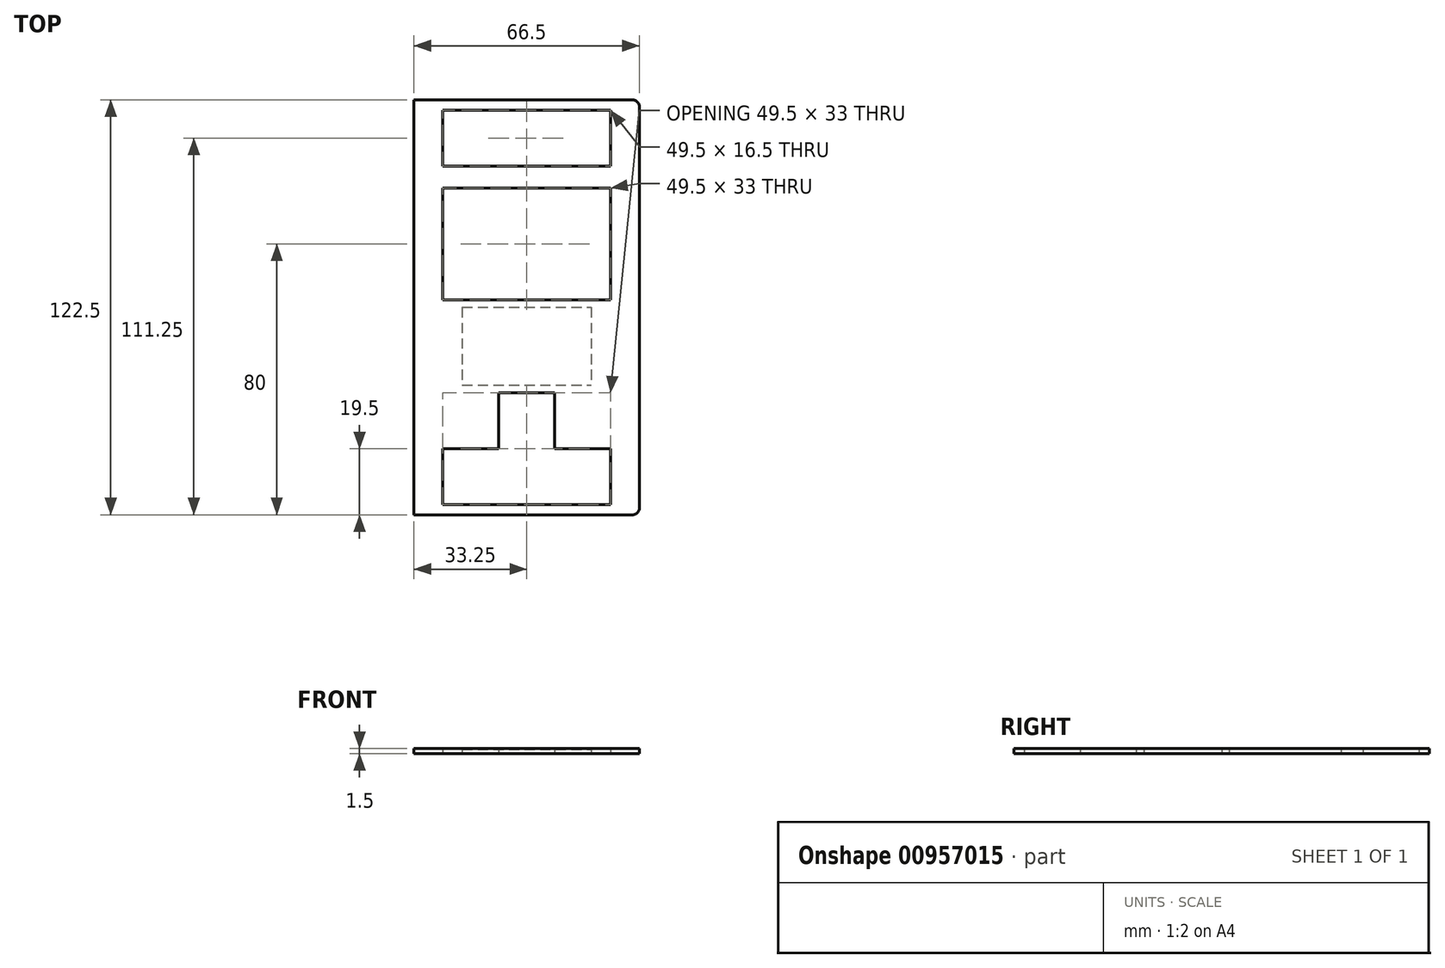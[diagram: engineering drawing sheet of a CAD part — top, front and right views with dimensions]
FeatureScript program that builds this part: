
annotation { "Feature Type Name" : "Feature", "Feature Type Description" : "" }
export const myFeature = defineFeature(function(context is Context, id is Id, definition is map)
    precondition{}
    {
        {
            var Q0;
            Q0=qCreatedBy(makeId("Top.planeOp"),FACE);
            var sketch = newSketch(context, id + "F0", { "sketchPlane" : qUnion([Q0])});
            skLineSegment(sketch, "E0.bottom", {"start": v(33.25, 61.25) * mm, "end": v(-33.25, 61.25) * mm});
            skLineSegment(sketch, "E0.top", {"start": v(33.25, -61.25) * mm, "end": v(-33.25, -61.25) * mm});
            skLineSegment(sketch, "E0.left", {"start": v(33.25, 61.25) * mm, "end": v(33.25, -61.25) * mm});
            skLineSegment(sketch, "E0.right", {"start": v(-33.25, 61.25) * mm, "end": v(-33.25, -61.25) * mm});
            skPoint(sketch, "E0.middle", {"position": v(0, 0) * mm});
            skLineSegment(sketch, "E1", {"start": v(0, -61.25) * mm, "end": v(0, -58.25) * mm});
            skLineSegment(sketch, "E2", {"start": v(0, -58.25) * mm, "end": v(24.75, -58.25) * mm});
            skLineSegment(sketch, "E3", {"start": v(0, -58.25) * mm, "end": v(-24.75, -58.25) * mm});
            skLineSegment(sketch, "E4", {"start": v(-24.75, -58.25) * mm, "end": v(-24.75, -41.75) * mm});
            skLineSegment(sketch, "E5", {"start": v(24.75, -58.25) * mm, "end": v(24.75, -41.75) * mm});
            skLineSegment(sketch, "E6", {"start": v(24.75, -41.75) * mm, "end": v(8.25, -41.75) * mm});
            skLineSegment(sketch, "E7", {"start": v(8.25, -41.75) * mm, "end": v(8.25, -25.25) * mm});
            skLineSegment(sketch, "E8", {"start": v(8.25, -25.25) * mm, "end": v(-8.25, -25.25) * mm});
            skLineSegment(sketch, "E9", {"start": v(-8.25, -25.25) * mm, "end": v(-8.25, -41.75) * mm});
            skLineSegment(sketch, "E10", {"start": v(-8.25, -41.75) * mm, "end": v(-24.75, -41.75) * mm});
            skLineSegment(sketch, "E11", {"start": v(0, 61.25) * mm, "end": v(0, 58.25) * mm});
            skLineSegment(sketch, "E12", {"start": v(0, 58.25) * mm, "end": v(-24.75, 58.25) * mm});
            skLineSegment(sketch, "E13", {"start": v(-24.75, 58.25) * mm, "end": v(-24.75, 41.75) * mm});
            skLineSegment(sketch, "E14", {"start": v(0, 58.25) * mm, "end": v(24.75, 58.25) * mm});
            skLineSegment(sketch, "E15", {"start": v(24.75, 58.25) * mm, "end": v(24.75, 41.75) * mm});
            skLineSegment(sketch, "E16", {"start": v(24.75, 41.75) * mm, "end": v(-24.75, 41.75) * mm});
            skLineSegment(sketch, "E17", {"start": v(0, 41.75) * mm, "end": v(0, 35.25) * mm});
            skLineSegment(sketch, "E18", {"start": v(0, 35.25) * mm, "end": v(-24.75, 35.25) * mm});
            skLineSegment(sketch, "E19", {"start": v(-24.75, 35.25) * mm, "end": v(-24.75, 2.25) * mm});
            skLineSegment(sketch, "E20", {"start": v(-24.75, 2.25) * mm, "end": v(24.75, 2.25) * mm});
            skLineSegment(sketch, "E21", {"start": v(24.75, 2.25) * mm, "end": v(24.75, 35.25) * mm});
            skLineSegment(sketch, "E22", {"start": v(24.75, 35.25) * mm, "end": v(0, 35.25) * mm});
            skSolve(sketch);
        }
        {
            var Q0;
            {var subQ7=sQuery(id+"F0.wireOp",EDGE,"E0.left");Q0=makeQuery(id+"F0.imprint","IMPRINT",FACE,{"disambiguationData":[TD([[makeQuery(id+"F0.imprint","IMPRINT",EDGE,{"derivedFrom":subQ7}),-1.0]])]});}
            extrude(context, id + "F1", {"entities" : qUnion([Q0]), "depth" : 1.5 * mm, "offsetDistance" : 25 * mm});
        }
        {
            var Q0;
            Q0=makeQuery(id+"F1.opExtrude","CAP_FACE",FACE,{"disambiguationData":[OSD([sQuery(id+"F0.wireOp",EDGE,"E0.bottom"),sQuery(id+"F0.wireOp",EDGE,"E0.top"),sQuery(id+"F0.wireOp",EDGE,"E0.left"),sQuery(id+"F0.wireOp",EDGE,"E0.right"),sQuery(id+"F0.wireOp",EDGE,"E2"),sQuery(id+"F0.wireOp",EDGE,"E3"),sQuery(id+"F0.wireOp",EDGE,"E4"),sQuery(id+"F0.wireOp",EDGE,"E5"),sQuery(id+"F0.wireOp",EDGE,"E6"),sQuery(id+"F0.wireOp",EDGE,"E7"),sQuery(id+"F0.wireOp",EDGE,"E8"),sQuery(id+"F0.wireOp",EDGE,"E9"),sQuery(id+"F0.wireOp",EDGE,"E10"),sQuery(id+"F0.wireOp",EDGE,"E12"),sQuery(id+"F0.wireOp",EDGE,"E13"),sQuery(id+"F0.wireOp",EDGE,"E14"),sQuery(id+"F0.wireOp",EDGE,"E15"),sQuery(id+"F0.wireOp",EDGE,"E16"),sQuery(id+"F0.wireOp",EDGE,"E18"),sQuery(id+"F0.wireOp",EDGE,"E19"),sQuery(id+"F0.wireOp",EDGE,"E20"),sQuery(id+"F0.wireOp",EDGE,"E21"),sQuery(id+"F0.wireOp",EDGE,"E22")])],"isStart":true});
            var sketch = newSketch(context, id + "F2", { "sketchPlane" : qUnion([Q0])});
            skLineSegment(sketch, "E23", {"start": v(0, 25.25) * mm, "end": v(0, -2.25) * mm});
            skLineSegment(sketch, "E24.bottom", {"start": v(-19, 0) * mm, "end": v(19, 0) * mm});
            skLineSegment(sketch, "E24.top", {"start": v(-19, 23) * mm, "end": v(19, 23) * mm});
            skLineSegment(sketch, "E24.left", {"start": v(-19, 0) * mm, "end": v(-19, 23) * mm});
            skLineSegment(sketch, "E24.right", {"start": v(19, 0) * mm, "end": v(19, 23) * mm});
            skPoint(sketch, "E24.middle", {"position": v(0, 11.5) * mm});
            skSolve(sketch);
        }
        {
            var Q0;
            {var subQ5=sQuery(id+"F2.wireOp",EDGE,"E24.right");Q0=makeQuery(id+"F2.imprint","IMPRINT",FACE,{"disambiguationData":[TD([[makeQuery(id+"F2.imprint","IMPRINT",EDGE,{"derivedFrom":subQ5}),1.0]])]});}
            var Q1;
            {var subQ5=sQuery(id+"F2.wireOp",EDGE,"E24.left");Q1=makeQuery(id+"F2.imprint","IMPRINT",FACE,{"disambiguationData":[TD([[makeQuery(id+"F2.imprint","IMPRINT",EDGE,{"derivedFrom":subQ5}),-1.0]])]});}
            extrude(context, id + "F3", {"entities" : qUnion([Q0, Q1]), "operationType" : NewBodyOperationType.REMOVE, "oppositeDirection" : true, "depth" : 1.2 * mm, "offsetDistance" : 25 * mm});
        }
        {
            var Q0;
            Q0=makeQuery(id+"F1.opExtrude","SWEPT_EDGE",EDGE,{"disambiguationData":[OSD([sQuery(id+"F0.wireOp",EDGE,"E0.top"),sQuery(id+"F0.wireOp",EDGE,"E0.left")])]});
            var Q1;
            Q1=makeQuery(id+"F1.opExtrude","SWEPT_EDGE",EDGE,{"disambiguationData":[OSD([sQuery(id+"F0.wireOp",EDGE,"E0.bottom"),sQuery(id+"F0.wireOp",EDGE,"E0.left")])]});
            fillet(context, id + "F4", {"entities" : qUnion([Q0, Q1]), "radius" : 2 * mm, "tangentPropagation" : true, "allowEdgeOverflow" : false});
        }
    });
